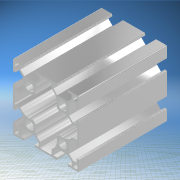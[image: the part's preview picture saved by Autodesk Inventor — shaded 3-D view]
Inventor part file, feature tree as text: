
AUTODESK INVENTOR PART (.ipt)
format: ipt  version: 2020.2 (Build 242310000, 310)  size: 481,280 bytes
history: native  units: mm
features: extrude x1, sketch x1
ambient origin geometry x8: Origin, YZ Plane, XZ Plane, XY Plane, X Axis, Y Axis, Z Axis, Center Point
bodies: Solid1 (feature_tree)
feature tree (2):
  extrude  "Extrusion1"  Depth=0.1mm
  sketch  "Sketch1"  dims[d0=9.9mm d1=4.0mm d2=4.0mm d3=0.1mm d4=0.1mm d5=9.9mm d6=0.1mm d7=0.1mm d8=80.0mm d9=0.0mm]
